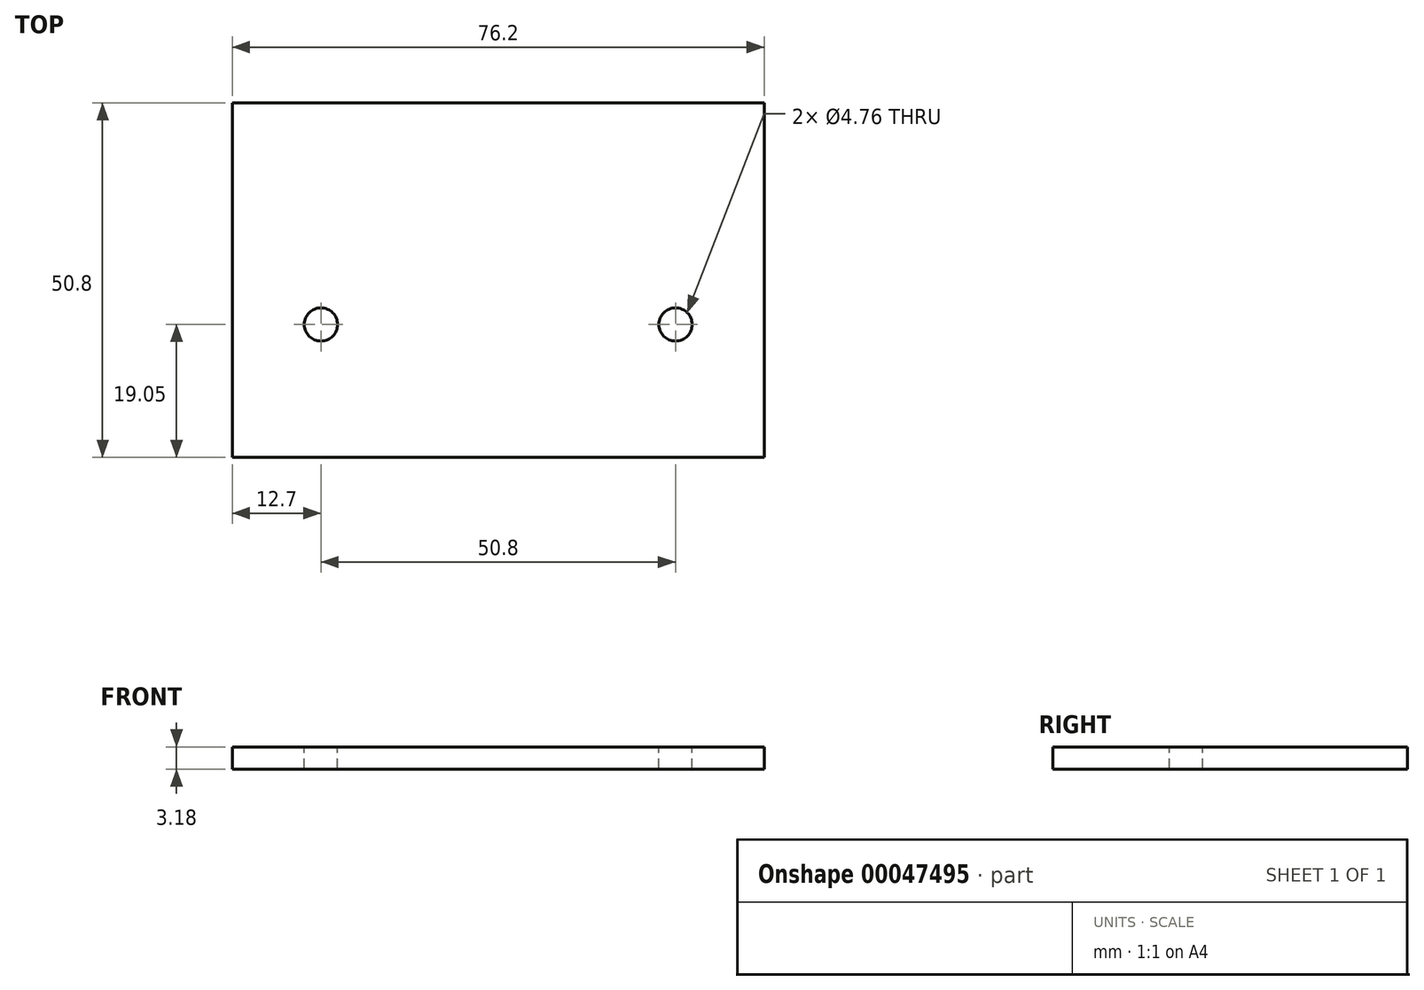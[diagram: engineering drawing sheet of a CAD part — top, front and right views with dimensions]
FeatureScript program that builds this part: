
annotation { "Feature Type Name" : "Feature", "Feature Type Description" : "" }
export const myFeature = defineFeature(function(context is Context, id is Id, definition is map)
    precondition{}
    {
        {
            var Q0;
            Q0=qCreatedBy(makeId("Top.planeOp"),FACE);
            var sketch = newSketch(context, id + "F0", { "sketchPlane" : qUnion([Q0])});
            skLineSegment(sketch, "E0.rect.bottom", {"start": v(38.1, 25.4) * mm, "end": v(-38.1, 25.4) * mm});
            skLineSegment(sketch, "E0.rect.top", {"start": v(38.1, -25.4) * mm, "end": v(-38.1, -25.4) * mm});
            skLineSegment(sketch, "E0.rect.left", {"start": v(38.1, 25.4) * mm, "end": v(38.1, -25.4) * mm});
            skLineSegment(sketch, "E0.rect.right", {"start": v(-38.1, 25.4) * mm, "end": v(-38.1, -25.4) * mm});
            skPoint(sketch, "E0.rect.middle", {"position": v(0, 0) * mm});
            skSolve(sketch);
        }
        {
            var Q0;
            Q0 = qSketchRegion(id + "F0", true);
            extrude(context, id + "F1", {"entities" : qUnion([Q0]), "depth" : 3.17 * mm, "symmetric" : true});
        }
        {
            var Q0;
            Q0=makeQuery(id+"F1.opExtrude","CAP_FACE",FACE,{"disambiguationData":[OSD([sQuery(id+"F0.wireOp",EDGE,"E0.rect.bottom"),sQuery(id+"F0.wireOp",EDGE,"E0.rect.top"),sQuery(id+"F0.wireOp",EDGE,"E0.rect.left"),sQuery(id+"F0.wireOp",EDGE,"E0.rect.right")])],"isStart":false});
            var sketch = newSketch(context, id + "F2", { "sketchPlane" : qUnion([Q0])});
            skCircle(sketch, "E1", {"center": v(-25.4, -6.35) * mm, "radius": 2.38 * mm});
            skCircle(sketch, "E2.MirrorC", {"center": v(25.4, -6.35) * mm, "radius": 2.38 * mm});
            skSolve(sketch);
        }
        {
            var Q0;
            Q0 = qSketchRegion(id + "F2", true);
            var Q1;
            Q1=makeQuery(id+"F1.opExtrude","CAP_FACE",FACE,{"disambiguationData":[OSD([sQuery(id+"F0.wireOp",EDGE,"E0.rect.bottom"),sQuery(id+"F0.wireOp",EDGE,"E0.rect.top"),sQuery(id+"F0.wireOp",EDGE,"E0.rect.left"),sQuery(id+"F0.wireOp",EDGE,"E0.rect.right")])],"isStart":true});
            extrude(context, id + "F3", {"entities" : qUnion([Q0]), "operationType" : NewBodyOperationType.REMOVE, "endBound" : BoundingType.UP_TO_SURFACE, "oppositeDirection" : true, "endBoundEntityFace" : qUnion([Q1]), "depth" : 25.4 * mm});
        }
    });
